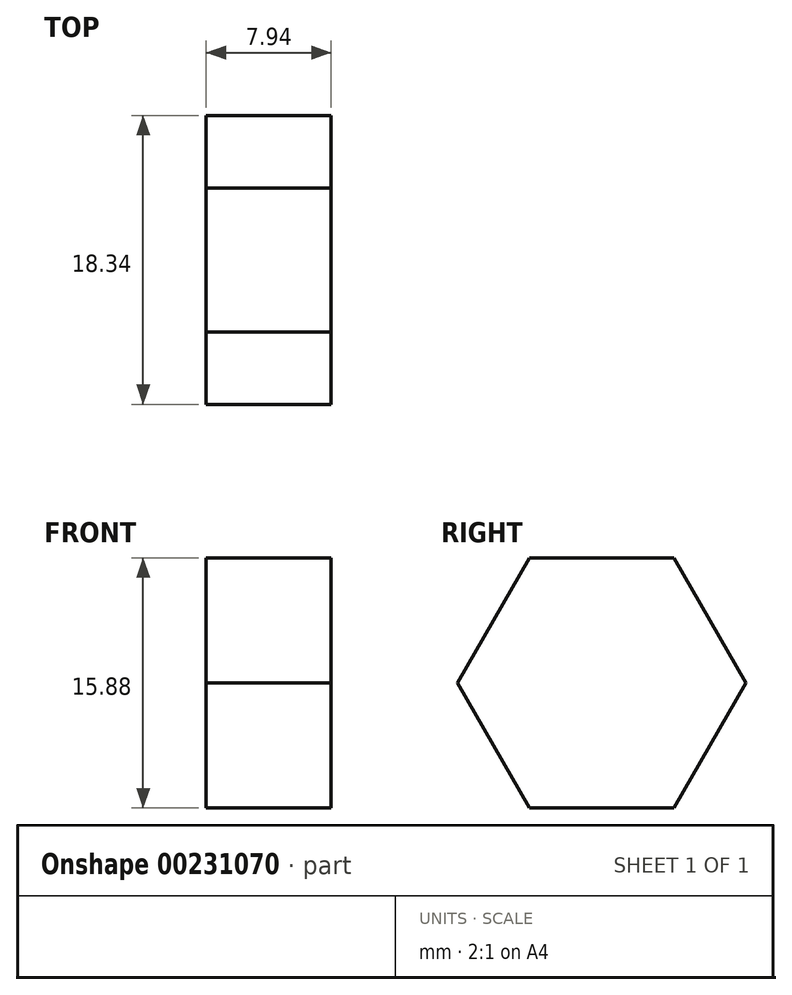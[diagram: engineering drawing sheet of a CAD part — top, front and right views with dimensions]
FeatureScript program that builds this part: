
annotation { "Feature Type Name" : "Feature", "Feature Type Description" : "" }
export const myFeature = defineFeature(function(context is Context, id is Id, definition is map)
    precondition{}
    {
        {
            var Q0;
            Q0=qCreatedBy(makeId("Right.planeOp"),FACE);
            var sketch = newSketch(context, id + "F0", { "sketchPlane" : qUnion([Q0])});
            skCircle(sketch, "E0.cCircle", {"center": v(0, 0) * mm, "radius": 7.94 * mm, "construction": true});
            skLineSegment(sketch, "E0.0", {"start": v(-4.58, 7.94) * mm, "end": v(4.58, 7.94) * mm});
            skLineSegment(sketch, "E0.1", {"start": v(4.58, 7.94) * mm, "end": v(9.17, 0) * mm});
            skLineSegment(sketch, "E0.2", {"start": v(9.17, 0) * mm, "end": v(4.58, -7.94) * mm});
            skLineSegment(sketch, "E0.3", {"start": v(4.58, -7.94) * mm, "end": v(-4.58, -7.94) * mm});
            skLineSegment(sketch, "E0.4", {"start": v(-4.58, -7.94) * mm, "end": v(-9.17, 0) * mm});
            skLineSegment(sketch, "E0.5", {"start": v(-9.17, 0) * mm, "end": v(-4.58, 7.94) * mm});
            skPoint(sketch, "E0.0.midPoint", {"position": v(0, 7.94) * mm});
            skSolve(sketch);
        }
        {
            var Q0;
            Q0 = qSketchRegion(id + "F0", true);
            extrude(context, id + "F1", {"entities" : qUnion([Q0]), "depth" : 7.94 * mm});
        }
    });
